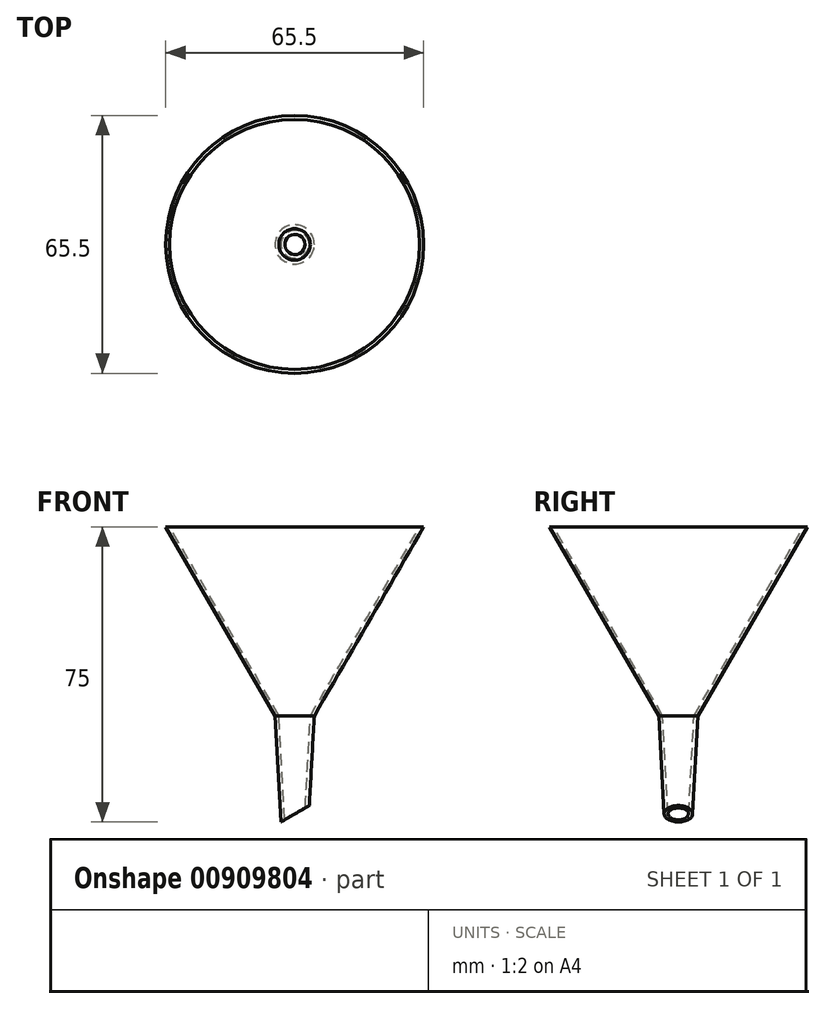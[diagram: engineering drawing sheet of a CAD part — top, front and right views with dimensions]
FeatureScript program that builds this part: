
annotation { "Feature Type Name" : "Feature", "Feature Type Description" : "" }
export const myFeature = defineFeature(function(context is Context, id is Id, definition is map)
    precondition{}
    {
        {
            var Q0;
            Q0=qCreatedBy(makeId("Top.planeOp"),FACE);
            var sketch = newSketch(context, id + "F0", { "sketchPlane" : qUnion([Q0])});
            skCircle(sketch, "E0", {"center": v(0, 0) * mm, "radius": 3.5 * mm});
            skSolve(sketch);
        }
        {
            var Q0;
            Q0=qCreatedBy(makeId("Top.planeOp"),FACE);
            cPlane(context, id + "F1", {"entities" : qUnion([Q0]), "cplaneType" : CPlaneType.OFFSET, "offset" : 27 * mm, "width" : 150 * mm, "height" : 150 * mm});
        }
        {
            var Q0;
            Q0=qCreatedBy(id+"F1.planeOp",FACE);
            var sketch = newSketch(context, id + "F2", { "sketchPlane" : qUnion([Q0])});
            skCircle(sketch, "E1", {"center": v(0, 0) * mm, "radius": 5 * mm});
            skSolve(sketch);
        }
        {
            var Q0;
            Q0=makeQuery(id+"F0.imprint","IMPRINT",FACE,{"disambiguationData":[TD([[makeQuery(id+"F0.imprint","IMPRINT",EDGE,{"derivedFrom":sQuery(id+"F0.wireOp",EDGE,"E0")}),1.0]])]});
            var Q1;
            Q1=makeQuery(id+"F2.imprint","IMPRINT",FACE,{"disambiguationData":[TD([[makeQuery(id+"F2.imprint","IMPRINT",EDGE,{"derivedFrom":sQuery(id+"F2.wireOp",EDGE,"E1")}),1.0]])]});
            loft(context, id + "F3", {"sheetProfilesArray" : [{ "sheetProfileEntities" : qUnion([Q0]) }, { "sheetProfileEntities" : qUnion([Q1]) }]});
        }
        {
            var Q0;
            Q0=qCreatedBy(makeId("Top.planeOp"),FACE);
            var sketch = newSketch(context, id + "F4", { "sketchPlane" : qUnion([Q0])});
            skCircle(sketch, "E2", {"center": v(0, 0) * mm, "radius": 2.5 * mm});
            skSolve(sketch);
        }
        {
            var Q0;
            Q0=qCreatedBy(id+"F1.planeOp",FACE);
            var sketch = newSketch(context, id + "F5", { "sketchPlane" : qUnion([Q0])});
            skCircle(sketch, "E3", {"center": v(0, 0) * mm, "radius": 4 * mm});
            skSolve(sketch);
        }
        {
            var Q1;
            Q1 = qSketchRegion(id + "F4", true);
            var Q2;
            Q2 = qSketchRegion(id + "F5", true);
            loft(context, id + "F6", {"operationType" : NewBodyOperationType.REMOVE, "sheetProfilesArray" : [{ "sheetProfileEntities" : qUnion([Q1]) }, { "sheetProfileEntities" : qUnion([Q2]) }]});
        }
        {
            var Q0;
            Q0=qCreatedBy(makeId("Front.planeOp"),FACE);
            var sketch = newSketch(context, id + "F7", { "sketchPlane" : qUnion([Q0])});
            skLineSegment(sketch, "E4", {"start": v(0, 0) * mm, "end": v(-3.5, 0) * mm, "construction": true});
            skLineSegment(sketch, "E5", {"start": v(-3.5, 0) * mm, "end": v(12.09, 9) * mm});
            skLineSegment(sketch, "E6", {"start": v(12.09, 9) * mm, "end": v(12.09, 0) * mm});
            skLineSegment(sketch, "E7", {"start": v(12.09, 0) * mm, "end": v(-3.5, 0) * mm});
            skSolve(sketch);
        }
        {
            var Q0;
            Q0=makeQuery(id+"F7.imprint","IMPRINT",FACE,{"disambiguationData":[TD([[makeQuery(id+"F7.imprint","IMPRINT",EDGE,{"derivedFrom":sQuery(id+"F7.wireOp",EDGE,"E5")}),-1.0]])]});
            extrude(context, id + "F8", {"entities" : qUnion([Q0]), "operationType" : NewBodyOperationType.REMOVE, "endBound" : BoundingType.SYMMETRIC, "depth" : 25 * mm, "offsetDistance" : 25 * mm});
        }
        {
            var Q0;
            Q0=qCreatedBy(id+"F1.planeOp",FACE);
            var sketch = newSketch(context, id + "F9", { "sketchPlane" : qUnion([Q0])});
            skCircle(sketch, "E8.1", {"center": v(0, 0) * mm, "radius": 4 * mm});
            skSolve(sketch);
        }
        {
            var Q0;
            Q0=qCreatedBy(id+"F1.planeOp",FACE);
            cPlane(context, id + "F10", {"entities" : qUnion([Q0]), "cplaneType" : CPlaneType.OFFSET, "offset" : 48 * mm, "width" : 150 * mm, "height" : 150 * mm});
        }
        {
            var Q0;
            Q0=qCreatedBy(id+"F10.planeOp",FACE);
            var sketch = newSketch(context, id + "F11", { "sketchPlane" : qUnion([Q0])});
            skCircle(sketch, "E9", {"center": v(0, 0) * mm, "radius": 31.75 * mm});
            skSolve(sketch);
        }
        {
            var Q0;
            Q0=qCreatedBy(id+"F1.planeOp",FACE);
            var sketch = newSketch(context, id + "F12", { "sketchPlane" : qUnion([Q0])});
            skCircle(sketch, "E10.0", {"center": v(0, 0) * mm, "radius": 5 * mm});
            skSolve(sketch);
        }
        {
            var Q0;
            Q0=qCreatedBy(id+"F10.planeOp",FACE);
            var sketch = newSketch(context, id + "F13", { "sketchPlane" : qUnion([Q0])});
            skCircle(sketch, "E11", {"center": v(0, 0) * mm, "radius": 32.75 * mm});
            skSolve(sketch);
        }
        {
            var Q1;
            Q1=makeQuery(id+"F12.imprint","IMPRINT",FACE,{"disambiguationData":[TD([[makeQuery(id+"F12.imprint","IMPRINT",EDGE,{"derivedFrom":sQuery(id+"F12.wireOp",EDGE,"E10.0")}),1.0]])]});
            var Q2;
            Q2=makeQuery(id+"F13.imprint","IMPRINT",FACE,{"disambiguationData":[TD([[makeQuery(id+"F13.imprint","IMPRINT",EDGE,{"derivedFrom":sQuery(id+"F13.wireOp",EDGE,"E11")}),1.0]])]});
            var Q3;
            Q3=sQuery(id+"F13.wireOp",EDGE,"E11");
            var Q4;
            Q4=sQuery(id+"F12.wireOp",EDGE,"E10.0");
            loft(context, id + "F14", {"operationType" : NewBodyOperationType.ADD, "sheetProfilesArray" : [{ "sheetProfileEntities" : qUnion([Q1]) }, { "sheetProfileEntities" : qUnion([Q2]) }], "wireProfilesArray" : [{ "wireProfileEntities" : qUnion([Q3]) }, { "wireProfileEntities" : qUnion([Q4]) }]});
        }
        {
            var Q1;
            Q1=makeQuery(id+"F9.imprint","IMPRINT",FACE,{"disambiguationData":[TD([[makeQuery(id+"F9.imprint","IMPRINT",EDGE,{"derivedFrom":sQuery(id+"F9.wireOp",EDGE,"E8.1")}),1.0]])]});
            var Q2;
            Q2=makeQuery(id+"F11.imprint","IMPRINT",FACE,{"disambiguationData":[TD([[makeQuery(id+"F11.imprint","IMPRINT",EDGE,{"derivedFrom":sQuery(id+"F11.wireOp",EDGE,"E9")}),1.0]])]});
            loft(context, id + "F15", {"operationType" : NewBodyOperationType.REMOVE, "sheetProfilesArray" : [{ "sheetProfileEntities" : qUnion([Q1]) }, { "sheetProfileEntities" : qUnion([Q2]) }]});
        }
    });
